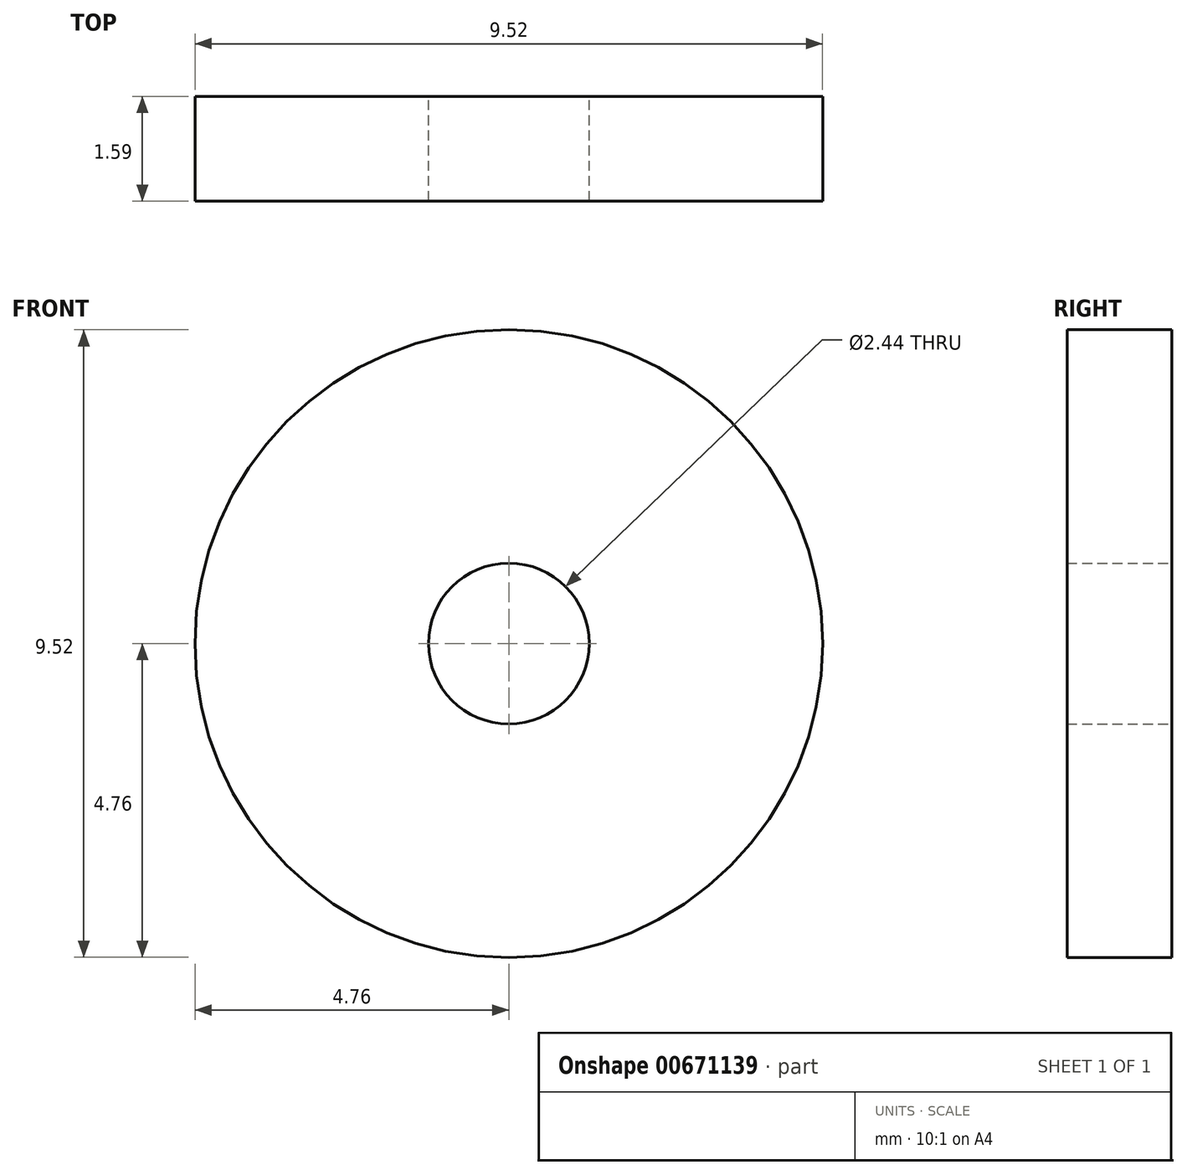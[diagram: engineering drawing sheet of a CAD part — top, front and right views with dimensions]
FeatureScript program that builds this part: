
annotation { "Feature Type Name" : "Feature", "Feature Type Description" : "" }
export const myFeature = defineFeature(function(context is Context, id is Id, definition is map)
    precondition{}
    {
        {
            var Q0;
            Q0=qCreatedBy(makeId("Front.planeOp"),FACE);
            var sketch = newSketch(context, id + "F0", { "sketchPlane" : qUnion([Q0])});
            skCircle(sketch, "E0", {"center": v(0, 0) * mm, "radius": 4.76 * mm});
            skCircle(sketch, "E1", {"center": v(0, 0) * mm, "radius": 1.22 * mm});
            skSolve(sketch);
        }
        {
            var Q0;
            Q0=qSketchRegion(id+"F0",true);
            extrude(context, id + "F1", {"entities" : qUnion([Q0]), "depth" : 1.59 * mm});
        }
    });
